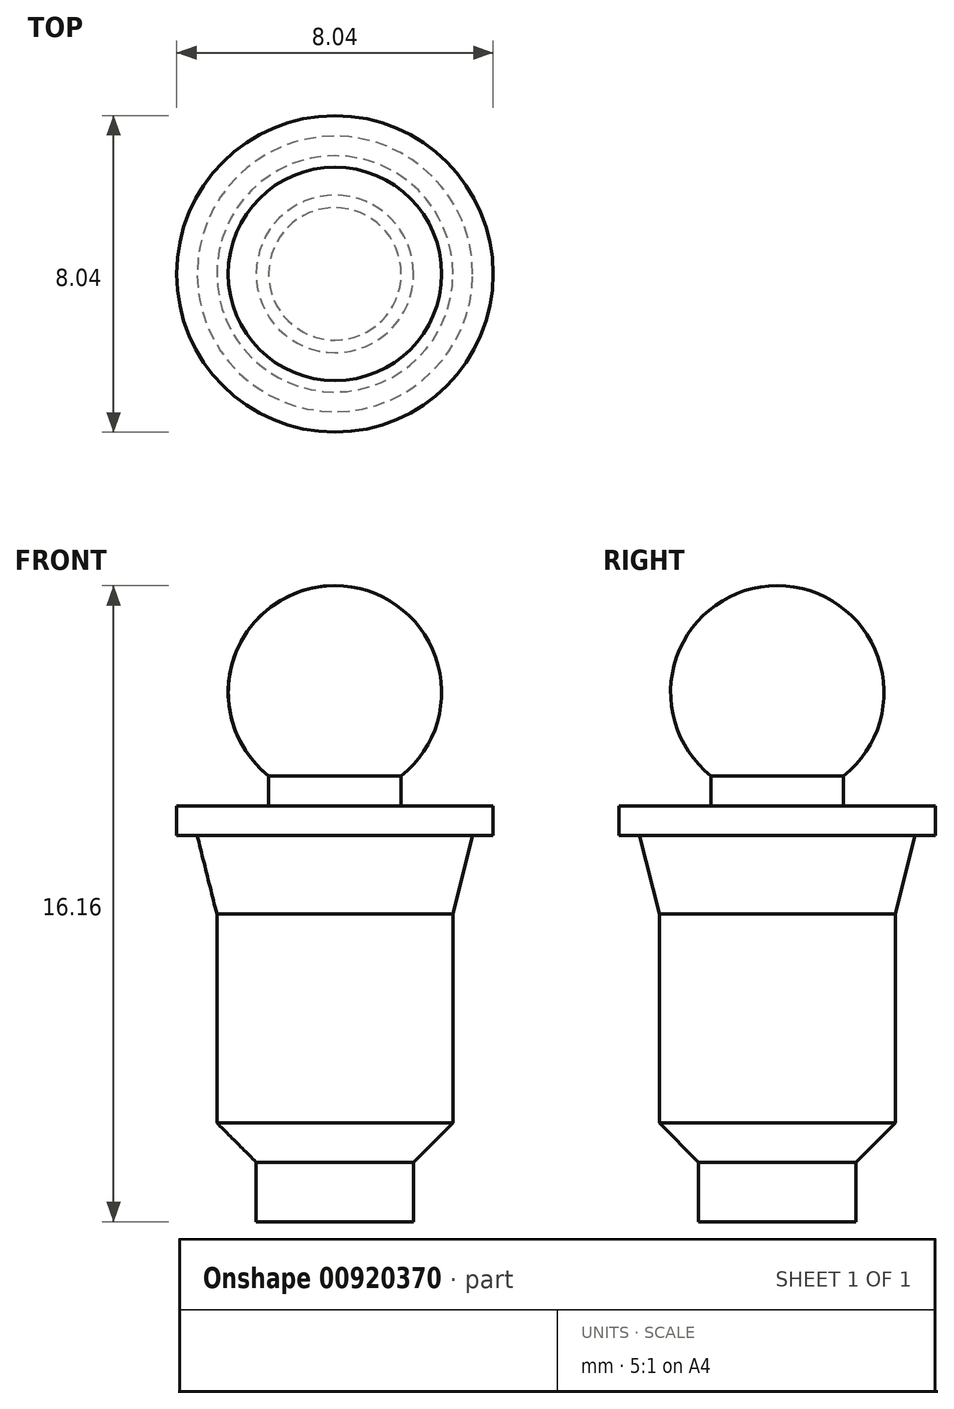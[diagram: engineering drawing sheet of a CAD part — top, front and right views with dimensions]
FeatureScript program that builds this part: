
annotation { "Feature Type Name" : "Feature", "Feature Type Description" : "" }
export const myFeature = defineFeature(function(context is Context, id is Id, definition is map)
    precondition{}
    {
        {
            var Q0;
            Q0=qCreatedBy(makeId("Front.planeOp"),FACE);
            var sketch = newSketch(context, id + "F0", { "sketchPlane" : qUnion([Q0])});
            skLineSegment(sketch, "E0", {"start": v(-4.7, -4.33) * mm, "end": v(-4.6, -4.33) * mm});
            skLineSegment(sketch, "E1", {"start": v(1.32, 8.67) * mm, "end": v(1.84, 8.67) * mm});
            skPoint(sketch, "E2.end.orphan", {"position": v(1.34, 1.2) * mm});
            skPoint(sketch, "E3.start.orphan", {"position": v(4.21, 1.2) * mm});
            skLineSegment(sketch, "E4", {"start": v(2.34, 1.36) * mm, "end": v(2.34, 6.67) * mm});
            skPoint(sketch, "E5.orphan", {"position": v(-2.16, -6.33) * mm});
            skPoint(sketch, "E6.first.point", {"position": v(-4.72, -5.33) * mm});
            skPoint(sketch, "E6.second.point", {"position": v(-5.16, -4.83) * mm});
            skPoint(sketch, "E6.third.point", {"position": v(-4.7, -4.33) * mm});
            skPoint(sketch, "E7.orphan", {"position": v(-5.16, -4.33) * mm});
            skPoint(sketch, "E8.orphan", {"position": v(-5.16, -5.33) * mm});
            skLineSegment(sketch, "E9", {"start": v(2.34, 6.67) * mm, "end": v(1.84, 8.67) * mm});
            skPoint(sketch, "E10.endSnap0", {"position": v(3.34, 1.28) * mm});
            skLineSegment(sketch, "E11", {"start": v(3.34, 0.36) * mm, "end": v(3.34, -1.15) * mm});
            skPoint(sketch, "E12.end.orphan", {"position": v(4.34, 1.2) * mm});
            skLineSegment(sketch, "E13", {"start": v(2.34, 1.36) * mm, "end": v(3.34, 0.36) * mm});
            skPoint(sketch, "E14.orphan", {"position": v(3.34, 0.58) * mm});
            skLineSegment(sketch, "E15", {"start": v(3.34, -1.15) * mm, "end": v(5.34, -1.15) * mm});
            skLineSegment(sketch, "E16", {"start": v(1.32, 8.67) * mm, "end": v(1.32, 9.42) * mm});
            skLineSegment(sketch, "E17", {"start": v(1.32, 9.42) * mm, "end": v(3.66, 9.42) * mm});
            skLineSegment(sketch, "E18", {"start": v(5.34, 9.42) * mm, "end": v(5.34, 9.42) * mm});
            skLineSegment(sketch, "E19", {"start": v(5.34, -1.15) * mm, "end": v(5.34, 9.42) * mm});
            skPoint(sketch, "E20.start.orphan", {"position": v(0.34, 5.67) * mm});
            skPoint(sketch, "E21.end.orphan", {"position": v(1.34, 3.67) * mm});
            skPoint(sketch, "E22.end.orphan", {"position": v(0.34, 1.67) * mm});
            skPoint(sketch, "E23.end.orphan", {"position": v(2.34, -0.33) * mm});
            skPoint(sketch, "E24.end.orphan", {"position": v(-2.16, -2.83) * mm});
            skPoint(sketch, "E25.orphan", {"position": v(-2.16, -4.33) * mm});
            skPoint(sketch, "E26.end.orphan", {"position": v(-4.16, -7.33) * mm});
            skPoint(sketch, "E26.start.orphan", {"position": v(-0.96, -7.33) * mm});
            skLineSegment(sketch, "E27", {"start": v(3.66, 9.42) * mm, "end": v(3.66, 10.17) * mm});
            skLineSegment(sketch, "E28", {"start": v(3.66, 10.17) * mm, "end": v(3.66, 10.17) * mm});
            skLineSegment(sketch, "E29", {"start": v(5.34, 10.26) * mm, "end": v(5.34, 9.42) * mm});
            skLineSegment(sketch, "E30", {"start": v(5.34, 10.26) * mm, "end": v(5.34, 13.18) * mm});
            skArc(sketch, "E31", {"start": v(5.34, 15.01) * mm, "mid": v(2.78, 13.2) * mm, "end": v(3.66, 10.17) * mm});
            skLineSegment(sketch, "E32", {"start": v(5.34, 13.18) * mm, "end": v(5.34, 15.01) * mm});
            skSolve(sketch);
        }
        {
            var Q0;
            Q0=makeQuery(id+"F0.imprint","IMPRINT",FACE,{"disambiguationData":[TD([[makeQuery(id+"F0.imprint","IMPRINT",EDGE,{"derivedFrom":sQuery(id+"F0.wireOp",EDGE,"E1")}),1.0]])]});
            var Q1;
            Q1=sQuery(id+"F0.wireOp",EDGE,"E19");
            revolve(context, id + "F1", {"surfaceOperationType" : NewSurfaceOperationType.NEW, "entities" : qUnion([Q0]), "axis" : qUnion([Q1]), "revolveType" : RevolveType.FULL});
        }
    });
